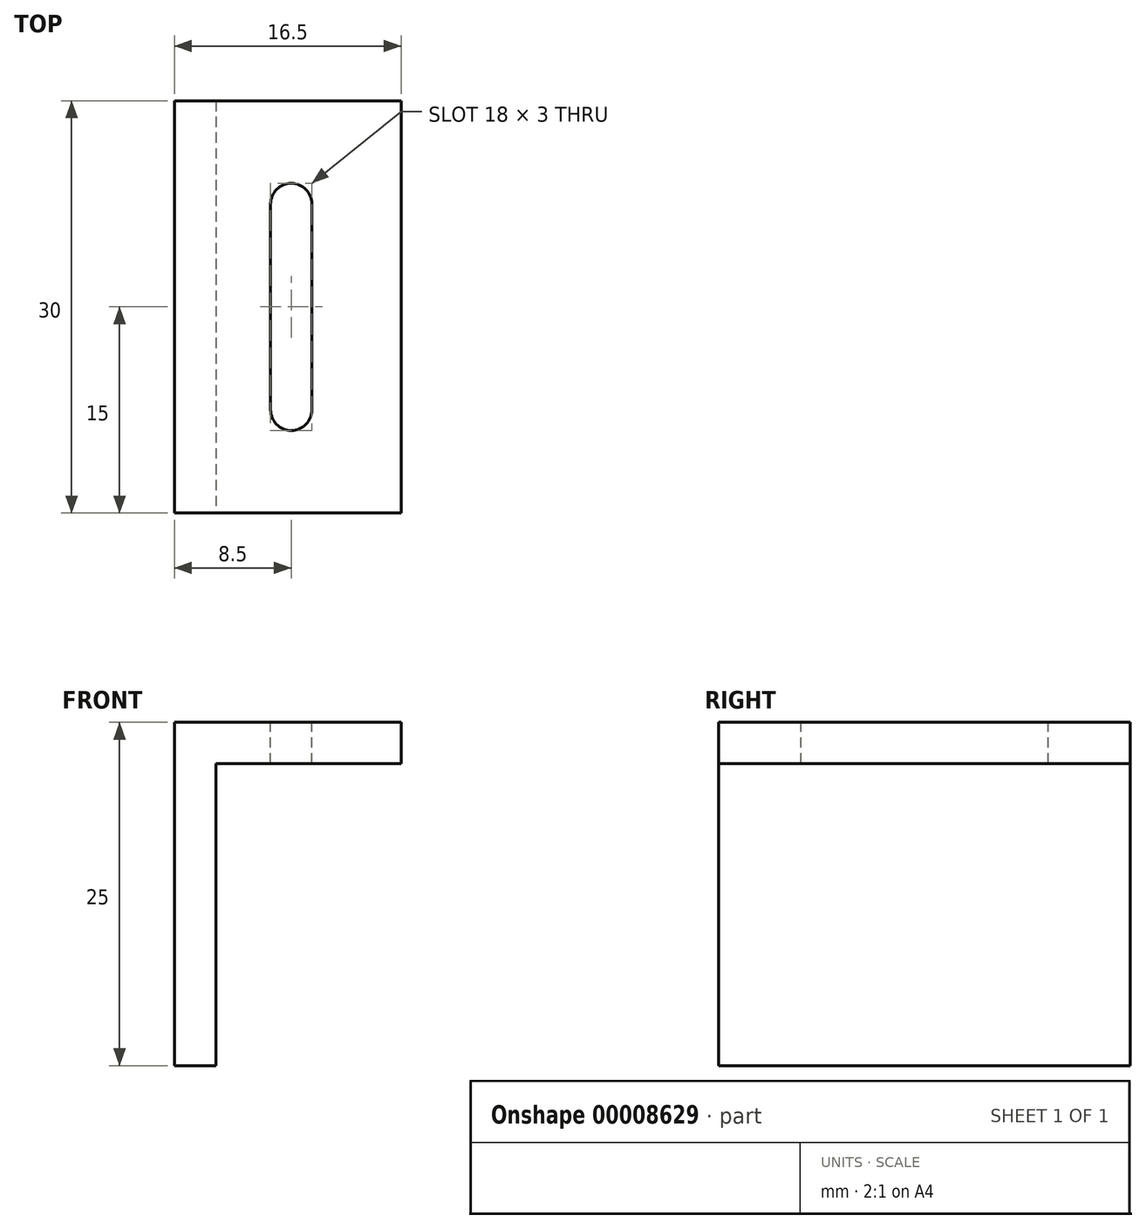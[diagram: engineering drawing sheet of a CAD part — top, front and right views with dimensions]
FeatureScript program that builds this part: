
annotation { "Feature Type Name" : "Feature", "Feature Type Description" : "" }
export const myFeature = defineFeature(function(context is Context, id is Id, definition is map)
    precondition{}
    {
        {
            var Q0;
            Q0=qCreatedBy(makeId("Top.planeOp"),FACE);
            var sketch = newSketch(context, id + "F0", { "sketchPlane" : qUnion([Q0])});
            skLineSegment(sketch, "E0.bottom", {"start": v(0, 0) * mm, "end": v(16.5, 0) * mm});
            skLineSegment(sketch, "E0.top", {"start": v(0, 30) * mm, "end": v(16.5, 30) * mm});
            skLineSegment(sketch, "E0.left", {"start": v(0, 0) * mm, "end": v(0, 30) * mm});
            skLineSegment(sketch, "E0.right", {"start": v(16.5, 0) * mm, "end": v(16.5, 30) * mm});
            skLineSegment(sketch, "E1", {"start": v(3, 30) * mm, "end": v(3, 0) * mm});
            skLineSegment(sketch, "E2", {"start": v(8.5, 30) * mm, "end": v(8.5, 0) * mm, "construction": true});
            skPoint(sketch, "E3", {"position": v(8.5, 15) * mm});
            skCircle(sketch, "E4", {"center": v(8.5, 22.5) * mm, "radius": 1.5 * mm});
            skCircle(sketch, "E5", {"center": v(8.5, 7.5) * mm, "radius": 1.5 * mm});
            skLineSegment(sketch, "E6", {"start": v(7, 22.5) * mm, "end": v(7, 7.5) * mm});
            skLineSegment(sketch, "E7", {"start": v(10, 22.5) * mm, "end": v(10, 7.5) * mm});
            skSolve(sketch);
        }
        {
            var Q0;
            {var subQ1=sQuery(id+"F0.wireOp",EDGE,"E0.right");Q0=makeQuery(id+"F0.imprint","IMPRINT",FACE,{"disambiguationData":[TD([[makeQuery(id+"F0.imprint","IMPRINT",EDGE,{"derivedFrom":subQ1}),1.0]])]});}
            extrude(context, id + "F1", {"entities" : qUnion([Q0]), "oppositeDirection" : true, "depth" : 3 * mm});
        }
        {
            var Q0;
            {var subQ0=sQuery(id+"F0.wireOp",EDGE,"E0.left");Q0=makeQuery(id+"F0.imprint","IMPRINT",FACE,{"disambiguationData":[TD([[makeQuery(id+"F0.imprint","IMPRINT",EDGE,{"derivedFrom":subQ0}),-1.0]])]});}
            extrude(context, id + "F2", {"entities" : qUnion([Q0]), "operationType" : NewBodyOperationType.ADD, "oppositeDirection" : true, "depth" : 25 * mm});
        }
    });
